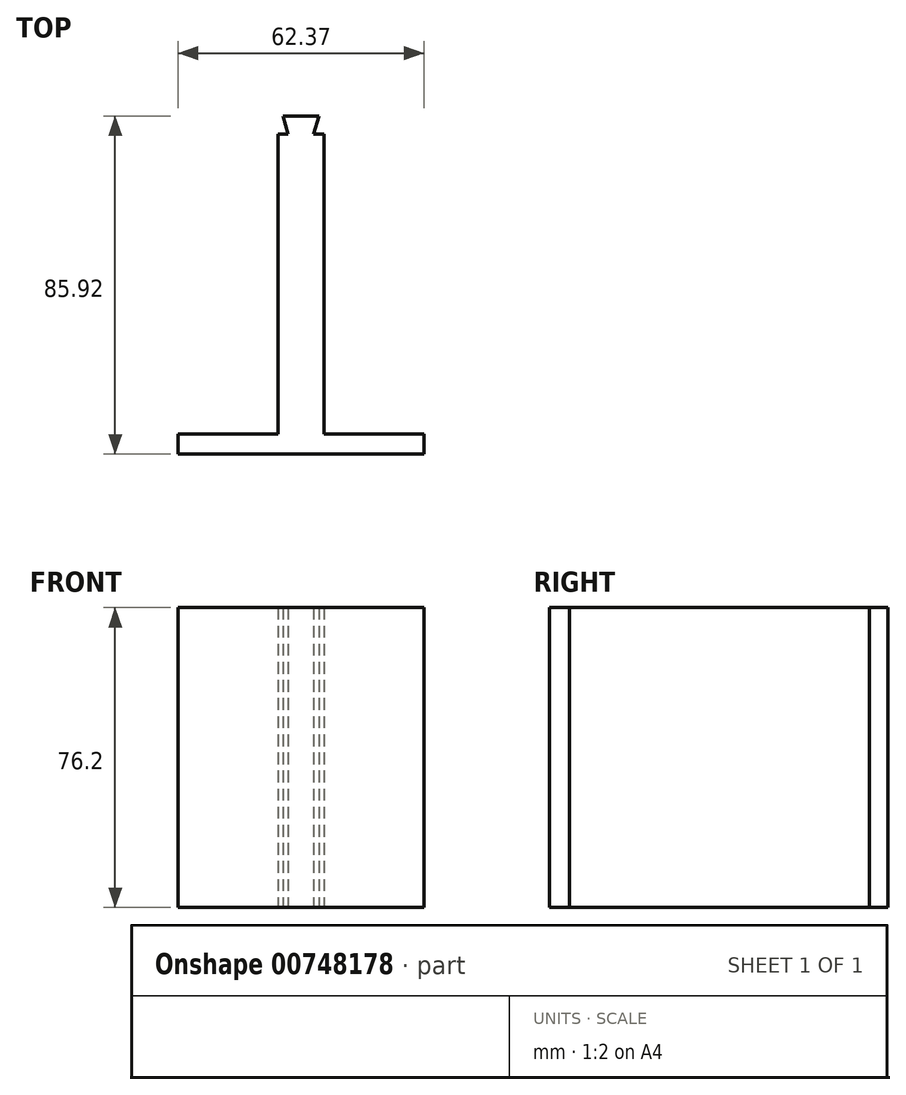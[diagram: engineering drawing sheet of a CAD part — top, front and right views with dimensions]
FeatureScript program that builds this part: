
annotation { "Feature Type Name" : "Feature", "Feature Type Description" : "" }
export const myFeature = defineFeature(function(context is Context, id is Id, definition is map)
    precondition{}
    {
        {
            var Q0;
            Q0=qCreatedBy(makeId("Top.planeOp"),FACE);
            var sketch = newSketch(context, id + "F0", { "sketchPlane" : qUnion([Q0])});
            skLineSegment(sketch, "E0", {"start": v(-1.33, 0) * mm, "end": v(7.82, 0) * mm});
            skLineSegment(sketch, "E1", {"start": v(7.82, 0) * mm, "end": v(6.49, -4.64) * mm});
            skLineSegment(sketch, "E2", {"start": v(6.49, -4.64) * mm, "end": v(9.03, -4.64) * mm});
            skLineSegment(sketch, "E3", {"start": v(9.03, -4.64) * mm, "end": v(9.03, -80.84) * mm});
            skLineSegment(sketch, "E4", {"start": v(9.03, -80.84) * mm, "end": v(34.43, -80.84) * mm});
            skLineSegment(sketch, "E5", {"start": v(34.43, -80.84) * mm, "end": v(34.43, -85.92) * mm});
            skLineSegment(sketch, "E6", {"start": v(34.43, -85.92) * mm, "end": v(-27.94, -85.92) * mm});
            skLineSegment(sketch, "E7", {"start": v(-27.94, -85.92) * mm, "end": v(-27.94, -80.84) * mm});
            skLineSegment(sketch, "E8", {"start": v(-27.94, -80.84) * mm, "end": v(-2.54, -80.84) * mm});
            skLineSegment(sketch, "E9", {"start": v(-2.54, -80.84) * mm, "end": v(-2.54, -4.64) * mm});
            skLineSegment(sketch, "E10", {"start": v(-2.54, -4.64) * mm, "end": v(0, -4.64) * mm});
            skLineSegment(sketch, "E11", {"start": v(0, -4.64) * mm, "end": v(-1.33, 0) * mm});
            skSolve(sketch);
        }
        {
            var Q0;
            Q0 = qSketchRegion(id + "F0", true);
            extrude(context, id + "F1", {"entities" : qUnion([Q0]), "endBound" : BoundingType.SYMMETRIC, "depth" : 76.2 * mm, "offsetDistance" : 25.4 * mm});
        }
        {
            var Q0;
            Q0=makeQuery(id+"F1.opExtrude","SWEPT_BODY",BODY,{"disambiguationData":[OSD([sQuery(id+"F0.wireOp",EDGE,"E0"),sQuery(id+"F0.wireOp",EDGE,"E1"),sQuery(id+"F0.wireOp",EDGE,"E2"),sQuery(id+"F0.wireOp",EDGE,"E3"),sQuery(id+"F0.wireOp",EDGE,"E4"),sQuery(id+"F0.wireOp",EDGE,"E5"),sQuery(id+"F0.wireOp",EDGE,"E6"),sQuery(id+"F0.wireOp",EDGE,"E7"),sQuery(id+"F0.wireOp",EDGE,"E8"),sQuery(id+"F0.wireOp",EDGE,"E9"),sQuery(id+"F0.wireOp",EDGE,"E10"),sQuery(id+"F0.wireOp",EDGE,"E11")])]});
            transform(context, id + "F2", {"entities" : qUnion([Q0]), "transformType" : TransformType.TRANSLATION_3D, "dx" : -4.06 * mm, "dy" : 44.96 * mm, "dz" : 0 * mm, "makeCopy" : false});
        }
    });
